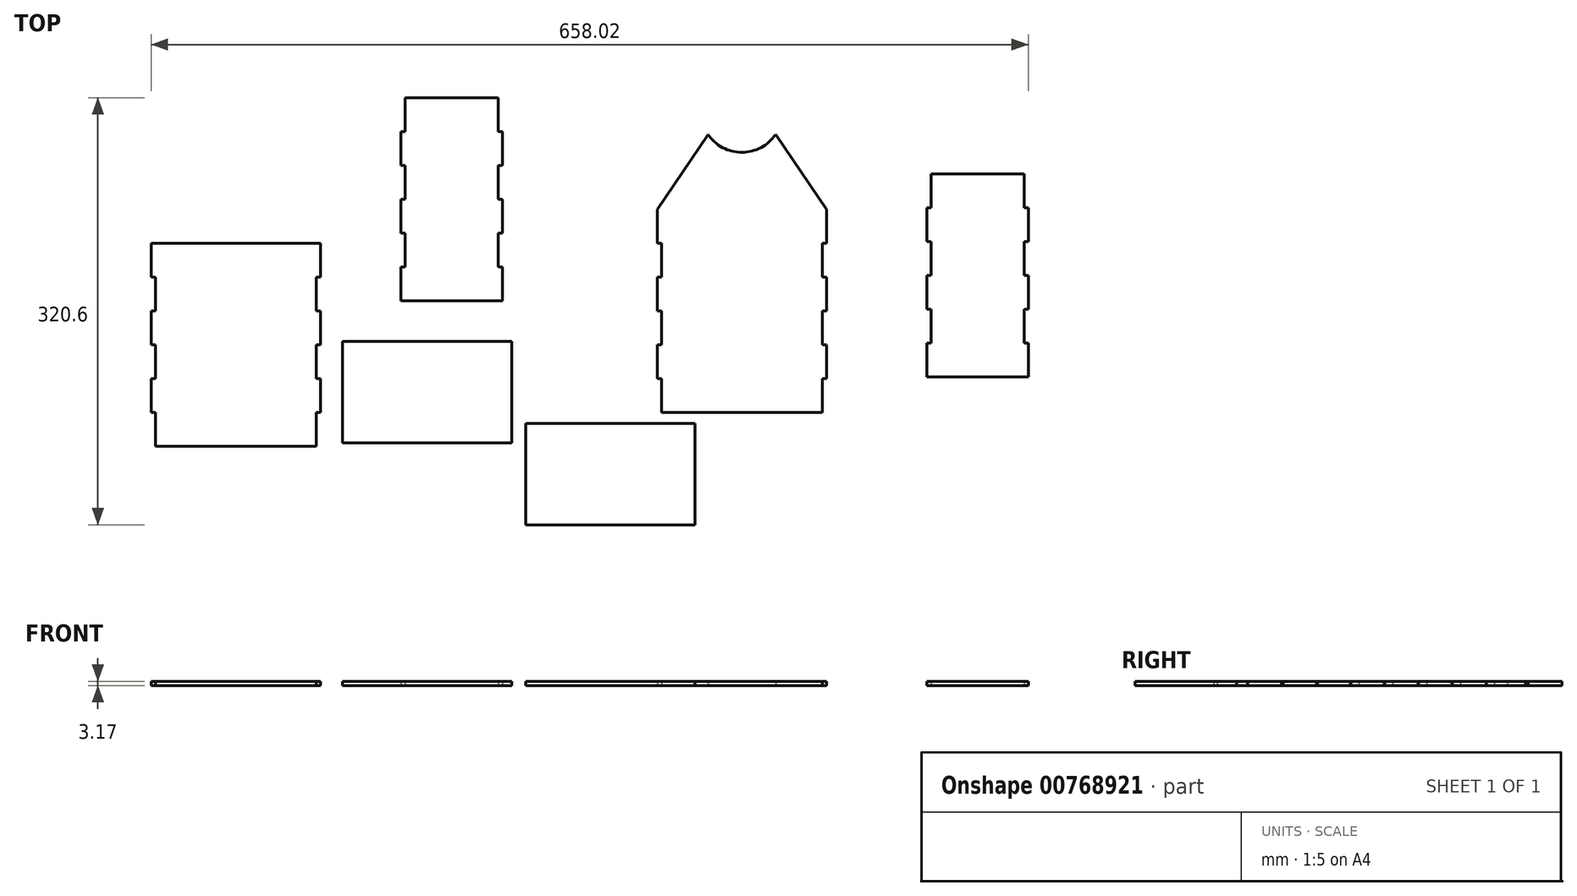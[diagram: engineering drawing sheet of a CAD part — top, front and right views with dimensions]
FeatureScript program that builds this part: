
annotation { "Feature Type Name" : "Feature", "Feature Type Description" : "" }
export const myFeature = defineFeature(function(context is Context, id is Id, definition is map)
    precondition{}
    {
        {
            var Q0;
            Q0=qCreatedBy(makeId("Top.planeOp"),FACE);
            var sketch = newSketch(context, id + "F0", { "sketchPlane" : qUnion([Q0])});
            skLineSegment(sketch, "E0.top", {"start": v(-123.82, 0) * mm, "end": v(-3.17, 0) * mm});
            skLineSegment(sketch, "E0.left", {"start": v(-127, 152.4) * mm, "end": v(-127, 127) * mm});
            skLineSegment(sketch, "E0.right", {"start": v(0, 152.4) * mm, "end": v(0, 127) * mm});
            skLineSegment(sketch, "E1.bottom", {"start": v(-316.23, 236.14) * mm, "end": v(-246.38, 236.14) * mm});
            skLineSegment(sketch, "E1.top", {"start": v(-319.4, 83.74) * mm, "end": v(-243.2, 83.74) * mm});
            skLineSegment(sketch, "E1.left", {"start": v(-319.4, 210.74) * mm, "end": v(-319.4, 185.34) * mm});
            skLineSegment(sketch, "E1.right", {"start": v(-243.2, 210.74) * mm, "end": v(-243.2, 185.34) * mm});
            skLineSegment(sketch, "E2.bottom", {"start": v(-225.51, -8.26) * mm, "end": v(-98.51, -8.26) * mm});
            skLineSegment(sketch, "E2.top", {"start": v(-225.51, -84.46) * mm, "end": v(-98.51, -84.46) * mm});
            skLineSegment(sketch, "E2.left", {"start": v(-225.51, -8.26) * mm, "end": v(-225.51, -84.46) * mm});
            skLineSegment(sketch, "E2.right", {"start": v(-98.51, -8.26) * mm, "end": v(-98.51, -84.46) * mm});
            skLineSegment(sketch, "E3", {"start": v(-127, 152.4) * mm, "end": v(-88.9, 208.67) * mm});
            skLineSegment(sketch, "E4", {"start": v(0, 152.4) * mm, "end": v(-38.1, 208.67) * mm});
            skArc(sketch, "E5.MirrorCS", {"start": v(-38.1, 208.67) * mm, "mid": v(-63.5, 195.2) * mm, "end": v(-88.9, 208.67) * mm});
            skLineSegment(sketch, "E6.bottom", {"start": v(-506.56, 127) * mm, "end": v(-379.56, 127) * mm});
            skLineSegment(sketch, "E6.top", {"start": v(-503.39, -25.4) * mm, "end": v(-382.74, -25.4) * mm});
            skLineSegment(sketch, "E6.left", {"start": v(-506.56, 127) * mm, "end": v(-506.56, 101.6) * mm});
            skLineSegment(sketch, "E6.right", {"start": v(-379.56, 127) * mm, "end": v(-379.56, 101.6) * mm});
            skLineSegment(sketch, "E7.bottom", {"start": v(-363.08, 53.32) * mm, "end": v(-236.08, 53.32) * mm});
            skLineSegment(sketch, "E7.top", {"start": v(-363.08, -22.88) * mm, "end": v(-236.08, -22.88) * mm});
            skLineSegment(sketch, "E7.left", {"start": v(-363.08, 53.32) * mm, "end": v(-363.08, -22.88) * mm});
            skLineSegment(sketch, "E7.right", {"start": v(-236.08, 53.32) * mm, "end": v(-236.08, -22.88) * mm});
            skLineSegment(sketch, "E8", {"start": v(-382.74, 101.6) * mm, "end": v(-382.74, 76.2) * mm});
            skLineSegment(sketch, "E9", {"start": v(-382.74, 76.2) * mm, "end": v(-379.56, 76.2) * mm});
            skLineSegment(sketch, "E10", {"start": v(-382.74, 50.8) * mm, "end": v(-379.56, 50.8) * mm});
            skLineSegment(sketch, "E11", {"start": v(-382.74, 25.4) * mm, "end": v(-379.56, 25.4) * mm});
            skLineSegment(sketch, "E12", {"start": v(-382.74, 0) * mm, "end": v(-379.56, 0) * mm});
            skLineSegment(sketch, "E13", {"start": v(-382.74, 101.6) * mm, "end": v(-379.56, 101.6) * mm});
            skLineSegment(sketch, "E14.trimOffspring", {"start": v(-379.56, 76.2) * mm, "end": v(-379.56, 50.8) * mm});
            skLineSegment(sketch, "E15.trimOffspring", {"start": v(-379.56, 25.4) * mm, "end": v(-379.56, 0) * mm});
            skLineSegment(sketch, "E16", {"start": v(-503.39, 101.6) * mm, "end": v(-503.39, 76.2) * mm});
            skLineSegment(sketch, "E17", {"start": v(-506.56, 101.6) * mm, "end": v(-503.39, 101.6) * mm});
            skLineSegment(sketch, "E18", {"start": v(-506.56, 76.2) * mm, "end": v(-503.39, 76.2) * mm});
            skLineSegment(sketch, "E19", {"start": v(-503.39, 50.8) * mm, "end": v(-506.56, 50.8) * mm});
            skLineSegment(sketch, "E20", {"start": v(-506.56, 25.4) * mm, "end": v(-503.39, 25.4) * mm});
            skLineSegment(sketch, "E21", {"start": v(-506.56, 0) * mm, "end": v(-503.39, 0) * mm});
            skLineSegment(sketch, "E22.trimOffspring", {"start": v(-506.56, 76.2) * mm, "end": v(-506.56, 50.8) * mm});
            skLineSegment(sketch, "E23.trimOffspring", {"start": v(-506.56, 25.4) * mm, "end": v(-506.56, 0) * mm});
            skLineSegment(sketch, "E24.trimOffspring", {"start": v(-382.74, 50.8) * mm, "end": v(-382.74, 25.4) * mm});
            skLineSegment(sketch, "E25.trimOffspring", {"start": v(-382.74, 0) * mm, "end": v(-382.74, -25.4) * mm});
            skLineSegment(sketch, "E26.trimOffspring", {"start": v(-503.39, 0) * mm, "end": v(-503.39, -25.4) * mm});
            skLineSegment(sketch, "E27.trimOffspring", {"start": v(-503.39, 50.8) * mm, "end": v(-503.39, 25.4) * mm});
            skPoint(sketch, "E28.orphan", {"position": v(-503.39, 127) * mm});
            skLineSegment(sketch, "E29", {"start": v(-246.38, 236.14) * mm, "end": v(-246.38, 210.74) * mm});
            skLineSegment(sketch, "E30", {"start": v(-316.23, 236.14) * mm, "end": v(-316.23, 210.74) * mm});
            skLineSegment(sketch, "E31", {"start": v(-246.38, 210.74) * mm, "end": v(-243.2, 210.74) * mm});
            skLineSegment(sketch, "E32", {"start": v(-246.38, 185.34) * mm, "end": v(-243.2, 185.34) * mm});
            skLineSegment(sketch, "E33", {"start": v(-246.38, 159.94) * mm, "end": v(-243.2, 159.94) * mm});
            skLineSegment(sketch, "E34", {"start": v(-246.38, 134.54) * mm, "end": v(-243.2, 134.54) * mm});
            skLineSegment(sketch, "E35", {"start": v(-246.38, 109.14) * mm, "end": v(-243.2, 109.14) * mm});
            skLineSegment(sketch, "E36", {"start": v(-319.4, 210.74) * mm, "end": v(-316.23, 210.74) * mm});
            skLineSegment(sketch, "E37", {"start": v(-319.4, 185.34) * mm, "end": v(-316.23, 185.34) * mm});
            skLineSegment(sketch, "E38", {"start": v(-319.4, 134.54) * mm, "end": v(-316.23, 134.54) * mm});
            skLineSegment(sketch, "E39", {"start": v(-319.4, 159.94) * mm, "end": v(-316.23, 159.94) * mm});
            skLineSegment(sketch, "E40", {"start": v(-319.4, 109.14) * mm, "end": v(-316.23, 109.14) * mm});
            skLineSegment(sketch, "E41.trimOffspring", {"start": v(-246.38, 185.34) * mm, "end": v(-246.38, 159.94) * mm});
            skLineSegment(sketch, "E42.trimOffspring", {"start": v(-316.23, 185.34) * mm, "end": v(-316.23, 159.94) * mm});
            skLineSegment(sketch, "E43.trimOffspring", {"start": v(-316.23, 134.54) * mm, "end": v(-316.23, 109.14) * mm});
            skLineSegment(sketch, "E44.trimOffspring", {"start": v(-246.38, 134.54) * mm, "end": v(-246.38, 109.14) * mm});
            skPoint(sketch, "E45.orphan", {"position": v(-316.23, 83.74) * mm});
            skLineSegment(sketch, "E46.trimOffspring", {"start": v(-243.2, 109.14) * mm, "end": v(-243.2, 83.74) * mm});
            skLineSegment(sketch, "E47.trimOffspring", {"start": v(-243.2, 159.94) * mm, "end": v(-243.2, 134.54) * mm});
            skLineSegment(sketch, "E48.trimOffspring", {"start": v(-319.4, 159.94) * mm, "end": v(-319.4, 134.54) * mm});
            skLineSegment(sketch, "E49.trimOffspring", {"start": v(-319.4, 109.14) * mm, "end": v(-319.4, 83.74) * mm});
            skLineSegment(sketch, "E50.bottom", {"start": v(78.43, 179.06) * mm, "end": v(148.28, 179.06) * mm});
            skLineSegment(sketch, "E50.top", {"start": v(75.26, 26.66) * mm, "end": v(151.46, 26.66) * mm});
            skLineSegment(sketch, "E50.left", {"start": v(75.26, 153.66) * mm, "end": v(75.26, 128.26) * mm});
            skLineSegment(sketch, "E50.right", {"start": v(151.46, 153.66) * mm, "end": v(151.46, 128.26) * mm});
            skLineSegment(sketch, "E51", {"start": v(148.28, 179.06) * mm, "end": v(148.28, 153.66) * mm});
            skLineSegment(sketch, "E52", {"start": v(78.43, 179.06) * mm, "end": v(78.43, 153.66) * mm});
            skLineSegment(sketch, "E53", {"start": v(148.28, 153.66) * mm, "end": v(151.46, 153.66) * mm});
            skLineSegment(sketch, "E54", {"start": v(148.28, 128.26) * mm, "end": v(151.46, 128.26) * mm});
            skLineSegment(sketch, "E55", {"start": v(148.28, 102.86) * mm, "end": v(151.46, 102.86) * mm});
            skLineSegment(sketch, "E56", {"start": v(148.28, 77.46) * mm, "end": v(151.46, 77.46) * mm});
            skLineSegment(sketch, "E57", {"start": v(148.28, 52.06) * mm, "end": v(151.46, 52.06) * mm});
            skLineSegment(sketch, "E58", {"start": v(75.26, 153.66) * mm, "end": v(78.43, 153.66) * mm});
            skLineSegment(sketch, "E59", {"start": v(75.26, 128.26) * mm, "end": v(78.43, 128.26) * mm});
            skLineSegment(sketch, "E60", {"start": v(75.26, 77.46) * mm, "end": v(78.43, 77.46) * mm});
            skLineSegment(sketch, "E61", {"start": v(75.26, 102.86) * mm, "end": v(78.43, 102.86) * mm});
            skLineSegment(sketch, "E62", {"start": v(75.26, 52.06) * mm, "end": v(78.43, 52.06) * mm});
            skLineSegment(sketch, "E63.trimOffspring", {"start": v(148.28, 128.26) * mm, "end": v(148.28, 102.86) * mm});
            skLineSegment(sketch, "E64.trimOffspring", {"start": v(78.43, 128.26) * mm, "end": v(78.43, 102.86) * mm});
            skLineSegment(sketch, "E65.trimOffspring", {"start": v(78.43, 77.46) * mm, "end": v(78.43, 52.06) * mm});
            skLineSegment(sketch, "E66.trimOffspring", {"start": v(148.28, 77.46) * mm, "end": v(148.28, 52.06) * mm});
            skPoint(sketch, "E67.orphan", {"position": v(78.43, 26.66) * mm});
            skLineSegment(sketch, "E68.trimOffspring", {"start": v(151.46, 52.06) * mm, "end": v(151.46, 26.66) * mm});
            skLineSegment(sketch, "E69.trimOffspring", {"start": v(151.46, 102.86) * mm, "end": v(151.46, 77.46) * mm});
            skLineSegment(sketch, "E70.trimOffspring", {"start": v(75.26, 102.86) * mm, "end": v(75.26, 77.46) * mm});
            skLineSegment(sketch, "E71.trimOffspring", {"start": v(75.26, 52.06) * mm, "end": v(75.26, 26.66) * mm});
            skLineSegment(sketch, "E72", {"start": v(-123.83, 127) * mm, "end": v(-123.83, 101.6) * mm});
            skLineSegment(sketch, "E73", {"start": v(-3.18, 127) * mm, "end": v(-3.18, 101.6) * mm});
            skLineSegment(sketch, "E74", {"start": v(-127, 127) * mm, "end": v(-123.83, 127) * mm});
            skLineSegment(sketch, "E75", {"start": v(-127, 101.6) * mm, "end": v(-123.83, 101.6) * mm});
            skLineSegment(sketch, "E76", {"start": v(-127, 76.2) * mm, "end": v(-123.82, 76.2) * mm});
            skLineSegment(sketch, "E77", {"start": v(-127, 50.8) * mm, "end": v(-123.82, 50.8) * mm});
            skLineSegment(sketch, "E78", {"start": v(-127, 25.4) * mm, "end": v(-123.82, 25.4) * mm});
            skLineSegment(sketch, "E79", {"start": v(-3.18, 127) * mm, "end": v(0, 127) * mm});
            skLineSegment(sketch, "E80", {"start": v(-3.18, 101.6) * mm, "end": v(0, 101.6) * mm});
            skLineSegment(sketch, "E81", {"start": v(-3.17, 76.2) * mm, "end": v(0, 76.2) * mm});
            skLineSegment(sketch, "E82", {"start": v(-3.17, 50.8) * mm, "end": v(0, 50.8) * mm});
            skLineSegment(sketch, "E83", {"start": v(-3.17, 25.4) * mm, "end": v(0, 25.4) * mm});
            skLineSegment(sketch, "E84.trimOffspring", {"start": v(0, 101.6) * mm, "end": v(0, 76.2) * mm});
            skLineSegment(sketch, "E85.trimOffspring", {"start": v(-3.17, 76.2) * mm, "end": v(-3.17, 0) * mm});
            skLineSegment(sketch, "E86.trimOffspring", {"start": v(0, 50.8) * mm, "end": v(0, 25.4) * mm});
            skPoint(sketch, "E87.orphan", {"position": v(0, 0) * mm});
            skPoint(sketch, "E88.orphan", {"position": v(-127, 0) * mm});
            skLineSegment(sketch, "E89.trimOffspring", {"start": v(-123.82, 25.4) * mm, "end": v(-123.82, 0) * mm});
            skLineSegment(sketch, "E90.trimOffspring", {"start": v(-127, 50.8) * mm, "end": v(-127, 25.4) * mm});
            skLineSegment(sketch, "E91.trimOffspring", {"start": v(-123.82, 76.2) * mm, "end": v(-123.82, 50.8) * mm});
            skLineSegment(sketch, "E92.trimOffspring", {"start": v(-127, 101.6) * mm, "end": v(-127, 76.2) * mm});
            skSolve(sketch);
        }
        {
            var Q0;
            Q0 = qSketchRegion(id + "F0", true);
            extrude(context, id + "F1", {"entities" : qUnion([Q0]), "depth" : 3.17 * mm, "offsetDistance" : 25.4 * mm});
        }
    });
